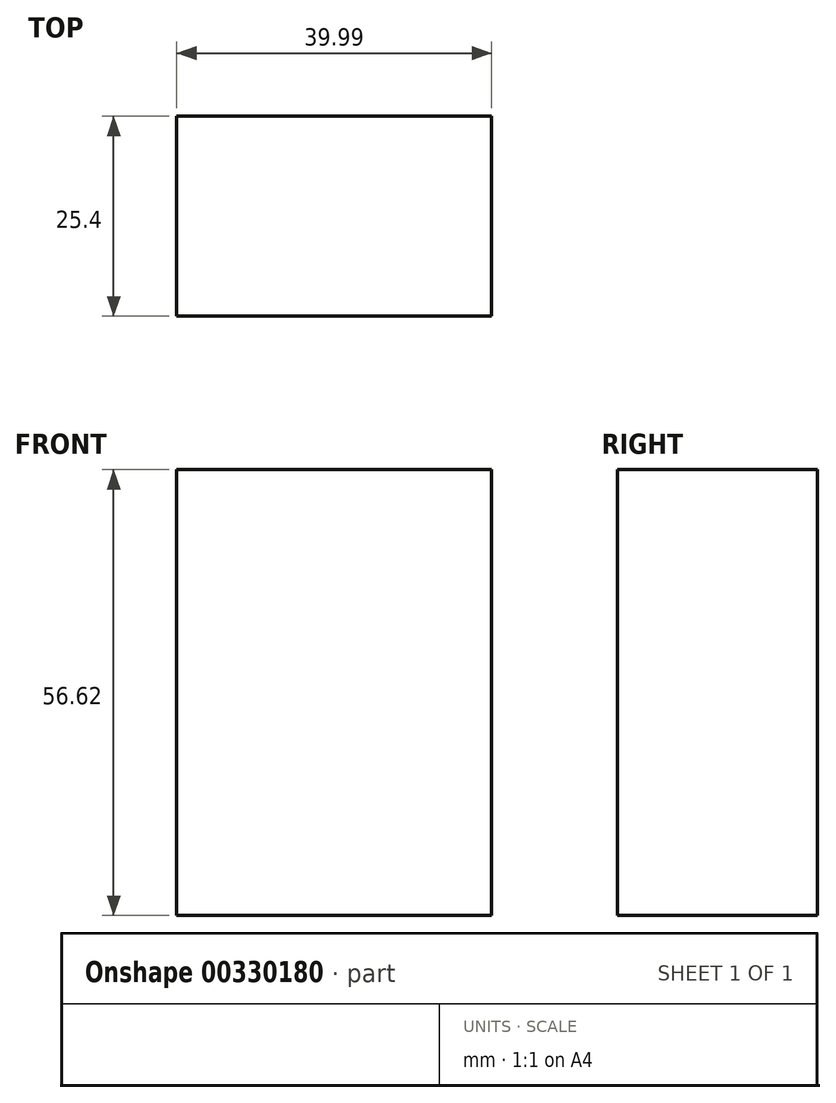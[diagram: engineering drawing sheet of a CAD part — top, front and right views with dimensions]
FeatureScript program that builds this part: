
annotation { "Feature Type Name" : "Feature", "Feature Type Description" : "" }
export const myFeature = defineFeature(function(context is Context, id is Id, definition is map)
    precondition{}
    {
        {
            var Q0;
            Q0=qCreatedBy(makeId("Front.planeOp"),FACE);
            var sketch = newSketch(context, id + "F0", { "sketchPlane" : qUnion([Q0])});
            skLineSegment(sketch, "E0.bottom", {"start": v(0, -36.17) * mm, "end": v(39.99, -36.17) * mm});
            skLineSegment(sketch, "E0.top", {"start": v(0, 20.45) * mm, "end": v(39.99, 20.45) * mm});
            skLineSegment(sketch, "E0.left", {"start": v(0, -36.17) * mm, "end": v(0, 20.45) * mm});
            skLineSegment(sketch, "E0.right", {"start": v(39.99, -36.17) * mm, "end": v(39.99, 20.45) * mm});
            skArc(sketch, "E1", {"start": v(39.99, 20.45) * mm, "mid": v(20, 40.44) * mm, "end": v(0, 20.45) * mm});
            skSolve(sketch);
        }
        {
            var Q0;
            Q0=makeQuery(id+"F0.imprint","IMPRINT",FACE,{"disambiguationData":[TD([[makeQuery(id+"F0.imprint","IMPRINT",EDGE,{"derivedFrom":sQuery(id+"F0.wireOp",EDGE,"E0.bottom")}),1.0]])]});
            extrude(context, id + "F1", {"entities" : qUnion([Q0]), "depth" : 25.4 * mm});
        }
    });
